# Revit family: Storage-Teknion-PLACW_Add_On_Storage_Cabinet_Wood-R2015
name_source: partatom
category: Furniture
revit_build: Autodesk Revit Architecture 2015 (Build: 20140323_1530(x64)
units: mm (PartAtom-declared; Revit-internal decimal feet)

## types (3) — shared parameters
Assembly Code = E2020200
Default Elevation = 48 "
Manufacturer = Teknion
Manufacturer Fax = 416.661.4586
Part Number = PLACW
Product Documentation Link = http://www.teknion.com
Product Line = Filing & Storage
Product Page URL = http://www.teknion.com
Series = Ledger Plus
Sustainability Data = http://www.teknion.com
Top Thickness = -1.0157 "
Top Thickness (inverse) = 1.0157 "
URL = www.teknion.com
Unit Weight URL = http://www.teknion.com
Warranty = http://www.teknion.com

## per-type parameters (varying)
| type | Description | Model |
| Above Worksurface | Add-On Storage Cabinet - Wood - Above Worksurface | PLACWA_ |
| Below Worksurface | Add-On Storage Cabinet - Wood - Below Worksurface | PLACWB_ |
| On Top of Storage | Add-On Storage Cabinet - Wood -On Top of Storage | PLACWC_ |

type visibility flags: 3 boolean params named "<type name>" — each type sets only its own to Yes (folded from table)

## geometry (parser evidence)
native form markers: Sweep x3
no freeform markers — native parametric forms only
